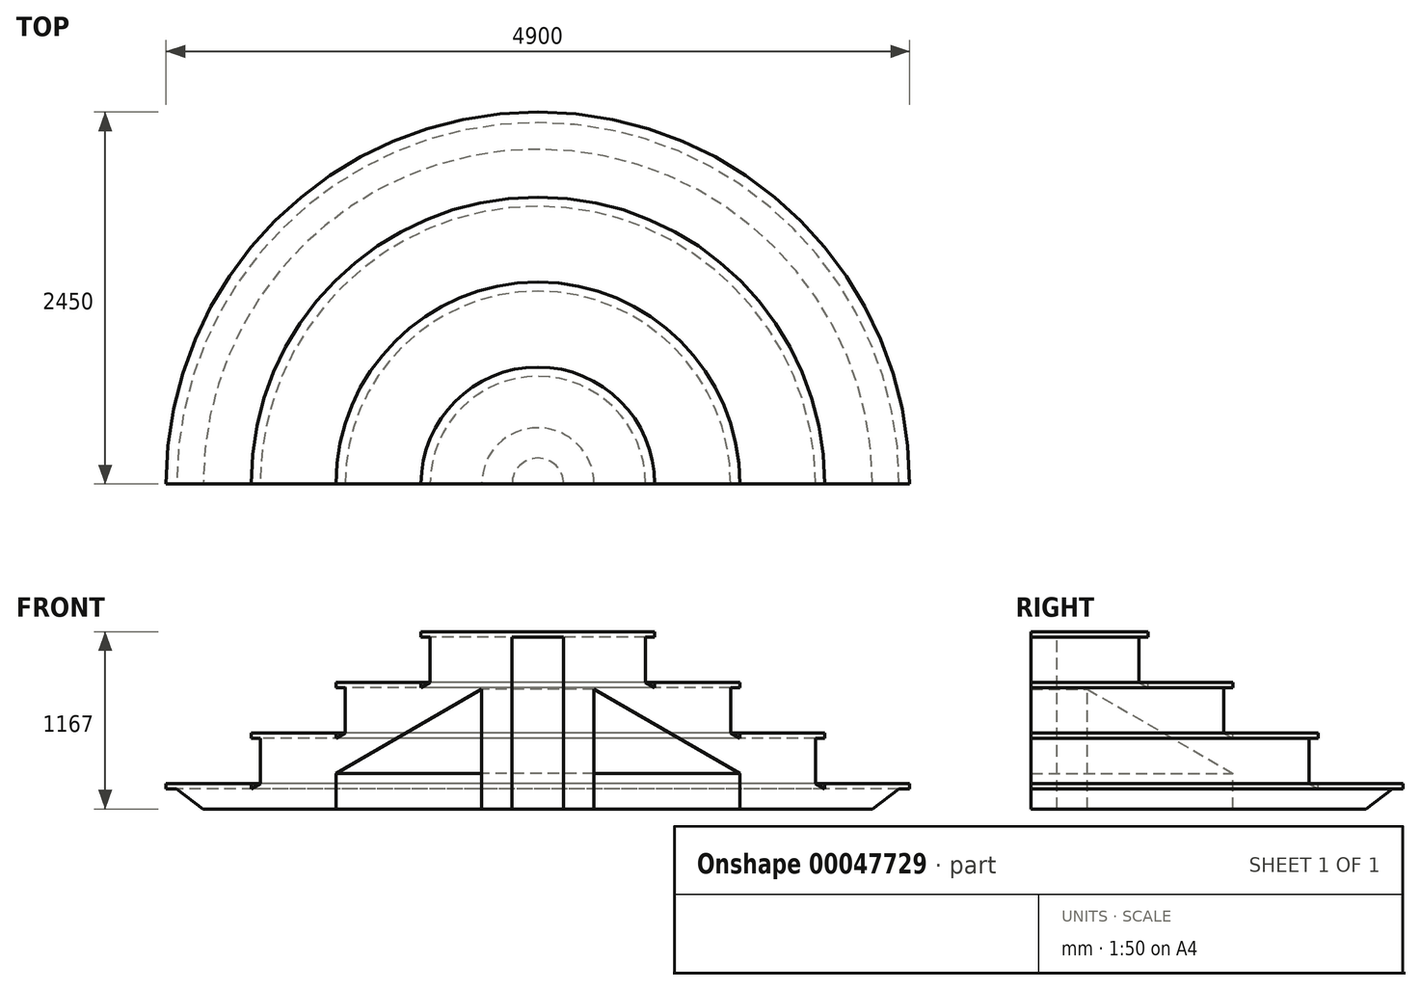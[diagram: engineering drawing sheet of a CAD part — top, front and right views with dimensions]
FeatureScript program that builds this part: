
annotation { "Feature Type Name" : "Feature", "Feature Type Description" : "" }
export const myFeature = defineFeature(function(context is Context, id is Id, definition is map)
    precondition{}
    {
        {
            var Q0;
            Q0=qCreatedBy(makeId("Front.planeOp"),FACE);
            var sketch = newSketch(context, id + "F0", { "sketchPlane" : qUnion([Q0])});
            skLineSegment(sketch, "E0.rect.bottom", {"start": v(1225, -583.5) * mm, "end": v(-1225, -583.5) * mm, "construction": true});
            skLineSegment(sketch, "E0.rect.top", {"start": v(1225, 583.5) * mm, "end": v(-1225, 583.5) * mm, "construction": true});
            skLineSegment(sketch, "E0.rect.left", {"start": v(1225, -583.5) * mm, "end": v(1225, 583.5) * mm, "construction": true});
            skLineSegment(sketch, "E0.rect.right", {"start": v(-1225, -583.5) * mm, "end": v(-1225, 583.5) * mm, "construction": true});
            skPoint(sketch, "E0.rect.middle", {"position": v(0, 0) * mm});
            skLineSegment(sketch, "E1.bottom", {"start": v(1225, 583.5) * mm, "end": v(455, 583.5) * mm});
            skLineSegment(sketch, "E1.top", {"start": v(1225, 548.5) * mm, "end": v(455, 548.5) * mm});
            skLineSegment(sketch, "E1.left", {"start": v(1225, 583.5) * mm, "end": v(1225, 548.5) * mm});
            skLineSegment(sketch, "E1.right", {"start": v(455, 583.5) * mm, "end": v(455, 548.5) * mm});
            skLineSegment(sketch, "E2.bottom", {"start": v(455, 250.5) * mm, "end": v(-105, 250.5) * mm});
            skLineSegment(sketch, "E2.top", {"start": v(455, 215.5) * mm, "end": v(-105, 215.5) * mm});
            skLineSegment(sketch, "E2.left", {"start": v(455, 250.5) * mm, "end": v(455, 215.5) * mm});
            skLineSegment(sketch, "E2.right", {"start": v(-105, 250.5) * mm, "end": v(-105, 215.5) * mm});
            skLineSegment(sketch, "E3.bottom", {"start": v(-105, -82.5) * mm, "end": v(-665, -82.5) * mm});
            skLineSegment(sketch, "E3.top", {"start": v(-105, -117.5) * mm, "end": v(-665, -117.5) * mm});
            skLineSegment(sketch, "E3.left", {"start": v(-105, -82.5) * mm, "end": v(-105, -117.5) * mm});
            skLineSegment(sketch, "E3.right", {"start": v(-665, -82.5) * mm, "end": v(-665, -117.5) * mm});
            skLineSegment(sketch, "E4.bottom", {"start": v(-665, -415.5) * mm, "end": v(-1225, -415.5) * mm});
            skLineSegment(sketch, "E4.top", {"start": v(-665, -450.5) * mm, "end": v(-1225, -450.5) * mm});
            skLineSegment(sketch, "E4.left", {"start": v(-665, -415.5) * mm, "end": v(-665, -450.5) * mm});
            skLineSegment(sketch, "E4.right", {"start": v(-1225, -415.5) * mm, "end": v(-1225, -450.5) * mm});
            skLineSegment(sketch, "E5", {"start": v(455, 215.5) * mm, "end": v(515.62, 250.5) * mm});
            skLineSegment(sketch, "E6", {"start": v(515.62, 250.5) * mm, "end": v(515.62, 548.5) * mm});
            skLineSegment(sketch, "E7", {"start": v(-105, -117.5) * mm, "end": v(-44.38, -82.5) * mm});
            skLineSegment(sketch, "E8", {"start": v(-44.38, -82.5) * mm, "end": v(-44.38, 215.5) * mm});
            skLineSegment(sketch, "E9", {"start": v(-665, -450.5) * mm, "end": v(-604.38, -415.5) * mm});
            skLineSegment(sketch, "E10", {"start": v(-604.38, -415.5) * mm, "end": v(-604.38, -117.5) * mm});
            skLineSegment(sketch, "E11", {"start": v(-1155, -450.5) * mm, "end": v(-980, -583.5) * mm});
            skLineSegment(sketch, "E12", {"start": v(-980, -583.5) * mm, "end": v(-105, -583.5) * mm});
            skLineSegment(sketch, "E13", {"start": v(-105, -583.5) * mm, "end": v(-105, -348.44) * mm});
            skLineSegment(sketch, "E14", {"start": v(1055, -583.5) * mm, "end": v(1055, 548.5) * mm});
            skLineSegment(sketch, "E15", {"start": v(-105, -348.44) * mm, "end": v(855, 205.82) * mm});
            skLineSegment(sketch, "E16", {"start": v(855, 205.82) * mm, "end": v(855, -583.5) * mm});
            skLineSegment(sketch, "E17", {"start": v(855, -583.5) * mm, "end": v(1055, -583.5) * mm});
            skSolve(sketch);
        }
        {
            var Q0;
            {var subQ7=sQuery(id+"F0.wireOp",EDGE,"E5");Q0=makeQuery(id+"F0.imprint","IMPRINT",FACE,{"disambiguationData":[TD([[makeQuery(id+"F0.imprint","IMPRINT",EDGE,{"derivedFrom":subQ7}),-1.0]])]});}
            var Q1;
            Q1=makeQuery(id+"F0.imprint","IMPRINT",FACE,{"disambiguationData":[TD([[makeQuery(id+"F0.imprint","IMPRINT",EDGE,{"derivedFrom":sQuery(id+"F0.wireOp",EDGE,"E4.bottom")}),1.0]])]});
            var Q2;
            Q2=makeQuery(id+"F0.imprint","IMPRINT",FACE,{"disambiguationData":[TD([[makeQuery(id+"F0.imprint","IMPRINT",EDGE,{"derivedFrom":sQuery(id+"F0.wireOp",EDGE,"E3.bottom")}),1.0]])]});
            var Q3;
            Q3=makeQuery(id+"F0.imprint","IMPRINT",FACE,{"disambiguationData":[TD([[makeQuery(id+"F0.imprint","IMPRINT",EDGE,{"derivedFrom":sQuery(id+"F0.wireOp",EDGE,"E2.bottom")}),1.0]])]});
            var Q4;
            Q4=makeQuery(id+"F0.imprint","IMPRINT",FACE,{"disambiguationData":[TD([[makeQuery(id+"F0.imprint","IMPRINT",EDGE,{"derivedFrom":sQuery(id+"F0.wireOp",EDGE,"E1.bottom")}),1.0]])]});
            var Q5;
            Q5=sQuery(id+"F0.wireOp",EDGE,"E1.left");
            revolve(context, id + "F1", {"entities" : qUnion([Q0, Q1, Q2, Q3, Q4]), "axis" : qUnion([Q5]), "revolveType" : RevolveType.ONE_DIRECTION, "angle" : 180 * degree});
        }
    });
